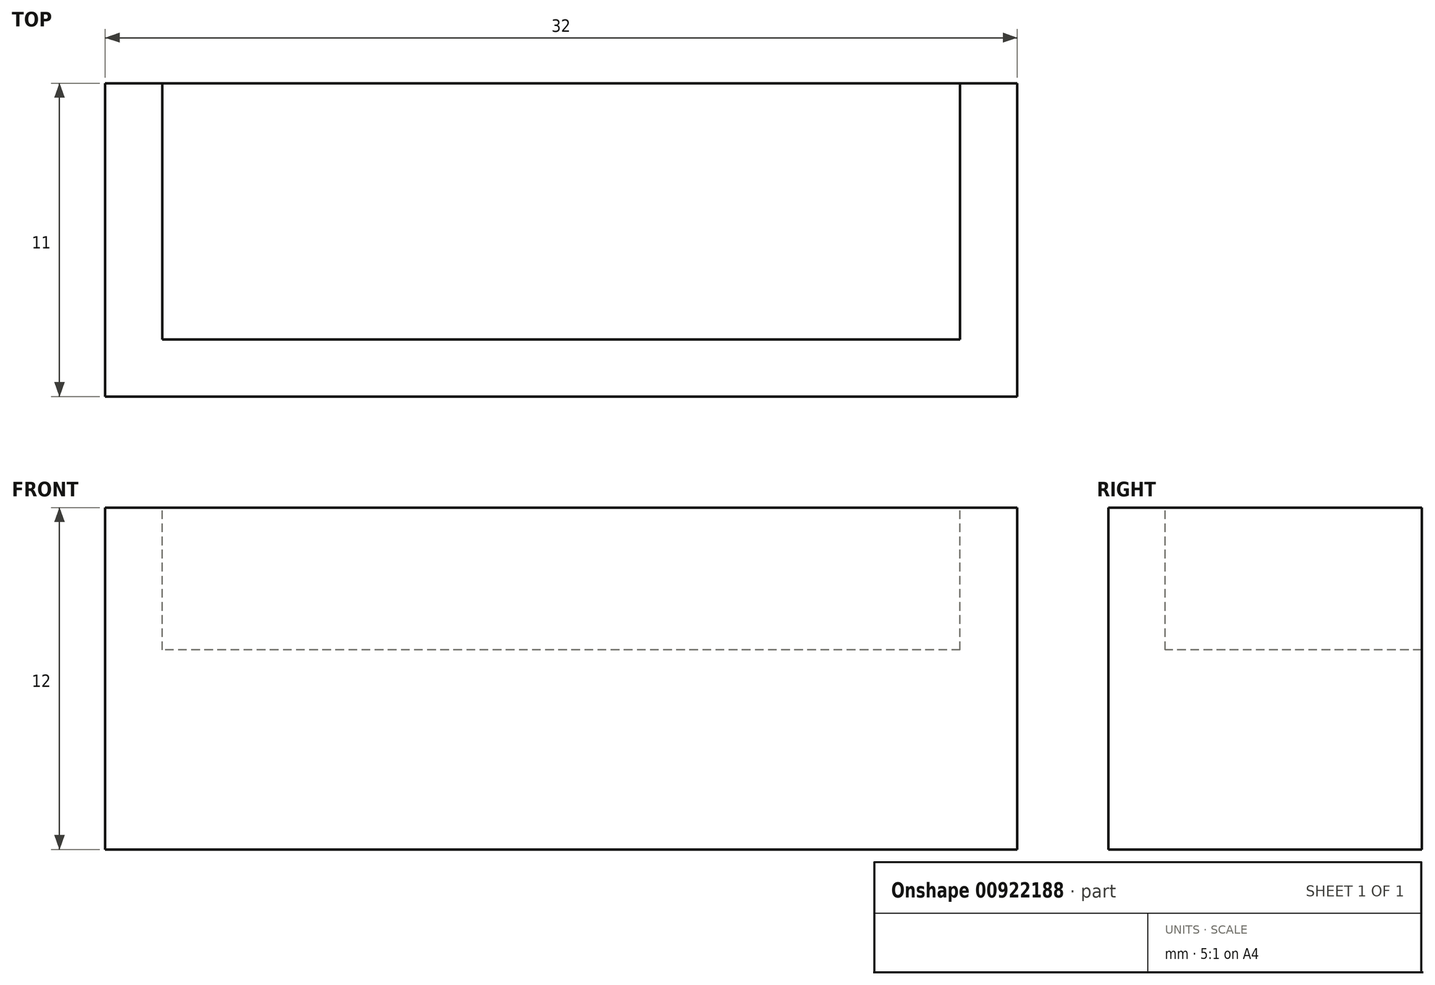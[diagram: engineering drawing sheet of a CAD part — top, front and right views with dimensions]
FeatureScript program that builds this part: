
annotation { "Feature Type Name" : "Feature", "Feature Type Description" : "" }
export const myFeature = defineFeature(function(context is Context, id is Id, definition is map)
    precondition{}
    {
        {
            var Q0;
            Q0=qCreatedBy(makeId("Front.planeOp"),FACE);
            var sketch = newSketch(context, id + "F0", { "sketchPlane" : qUnion([Q0])});
            skLineSegment(sketch, "E0.bottom", {"start": v(16, -6) * mm, "end": v(-16, -6) * mm});
            skLineSegment(sketch, "E0.top", {"start": v(16, 6) * mm, "end": v(-16, 6) * mm});
            skLineSegment(sketch, "E0.left", {"start": v(16, -6) * mm, "end": v(16, 6) * mm});
            skLineSegment(sketch, "E0.right", {"start": v(-16, -6) * mm, "end": v(-16, 6) * mm});
            skPoint(sketch, "E0.middle", {"position": v(0, 0) * mm});
            skSolve(sketch);
        }
        {
            var Q0;
            Q0=makeQuery(id+"F0.imprint","IMPRINT",FACE,{"disambiguationData":[TD([[makeQuery(id+"F0.imprint","IMPRINT",EDGE,{"derivedFrom":sQuery(id+"F0.wireOp",EDGE,"E0.bottom")}),-1.0]])]});
            extrude(context, id + "F1", {"entities" : qUnion([Q0]), "depth" : 11 * mm, "offsetDistance" : 25 * mm});
        }
        {
            var Q0;
            Q0=makeQuery(id+"F1.opExtrude","SWEPT_FACE",FACE,{"disambiguationData":[OSD([sQuery(id+"F0.wireOp",EDGE,"E0.top")])]});
            var sketch = newSketch(context, id + "F2", { "sketchPlane" : qUnion([Q0])});
            skLineSegment(sketch, "E1.bottom", {"start": v(-14, 0) * mm, "end": v(14, 0) * mm});
            skLineSegment(sketch, "E1.top", {"start": v(-14, -9) * mm, "end": v(14, -9) * mm});
            skLineSegment(sketch, "E1.left", {"start": v(-14, 0) * mm, "end": v(-14, -9) * mm});
            skLineSegment(sketch, "E1.right", {"start": v(14, 0) * mm, "end": v(14, -9) * mm});
            skSolve(sketch);
        }
        {
            var Q0;
            Q0=makeQuery(id+"F2.imprint","IMPRINT",FACE,{"disambiguationData":[TD([[makeQuery(id+"F2.imprint","IMPRINT",EDGE,{"derivedFrom":sQuery(id+"F2.wireOp",EDGE,"E1.bottom")}),1.0]])]});
            extrude(context, id + "F3", {"entities" : qUnion([Q0]), "operationType" : NewBodyOperationType.REMOVE, "oppositeDirection" : true, "depth" : 5 * mm, "offsetDistance" : 25 * mm});
        }
    });
